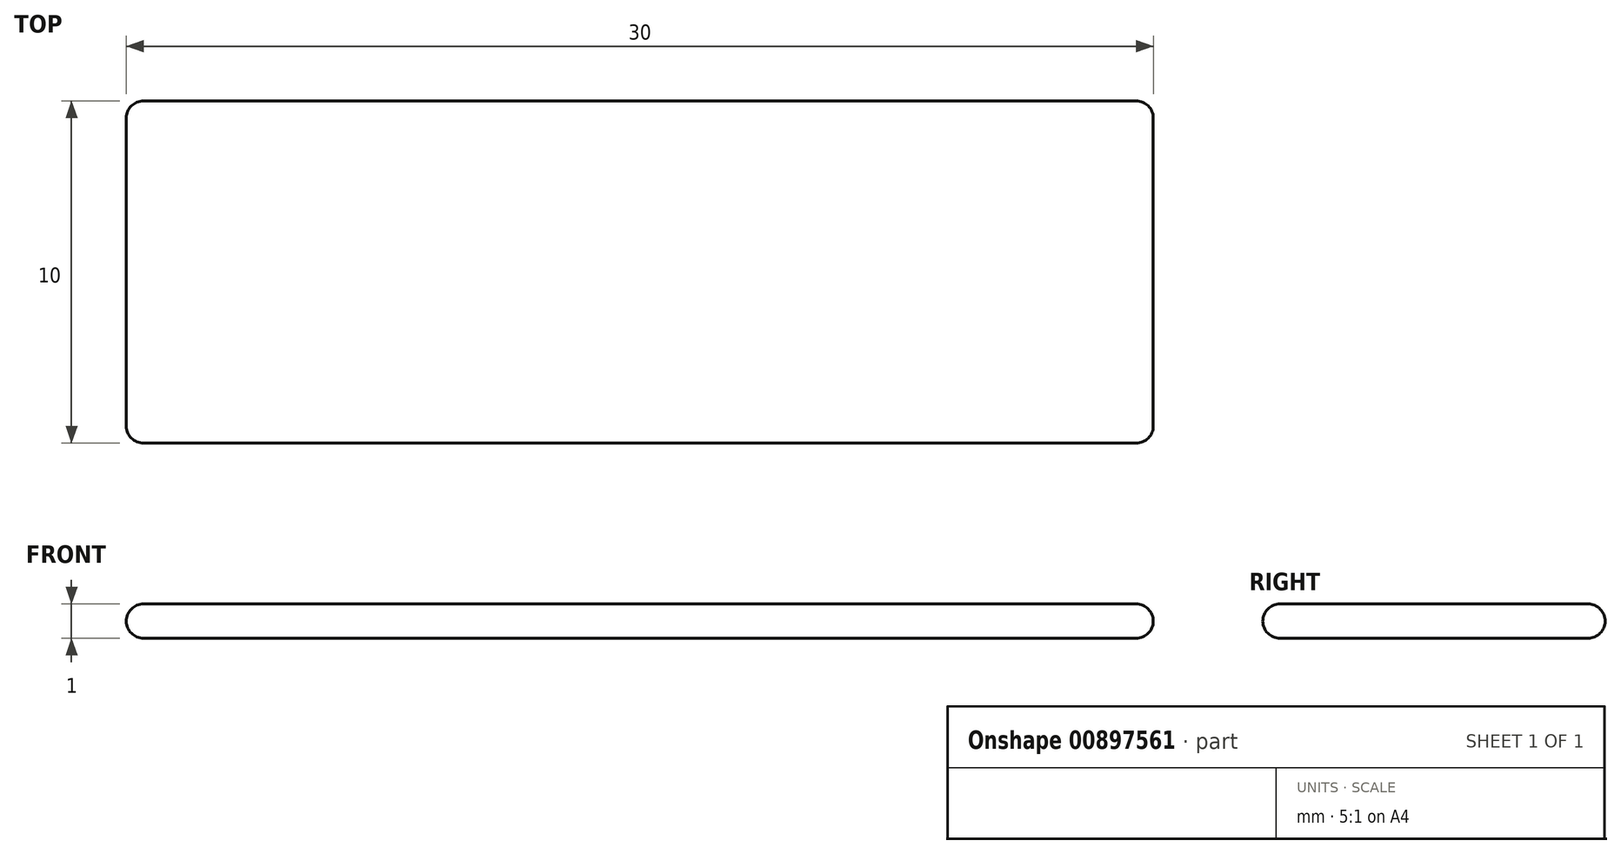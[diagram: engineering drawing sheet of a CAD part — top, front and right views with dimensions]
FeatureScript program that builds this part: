
annotation { "Feature Type Name" : "Feature", "Feature Type Description" : "" }
export const myFeature = defineFeature(function(context is Context, id is Id, definition is map)
    precondition{}
    {
        {
            var Q0;
            Q0=qCreatedBy(makeId("Top.planeOp"),FACE);
            var sketch = newSketch(context, id + "F0", { "sketchPlane" : qUnion([Q0])});
            skLineSegment(sketch, "E0.bottom", {"start": v(-49.18, 35.23) * mm, "end": v(-19.18, 35.23) * mm});
            skLineSegment(sketch, "E0.top", {"start": v(-49.18, 25.23) * mm, "end": v(-19.18, 25.23) * mm});
            skLineSegment(sketch, "E0.left", {"start": v(-49.18, 35.23) * mm, "end": v(-49.18, 25.23) * mm});
            skLineSegment(sketch, "E0.right", {"start": v(-19.18, 35.23) * mm, "end": v(-19.18, 25.23) * mm});
            skSolve(sketch);
        }
        {
            var Q0;
            Q0 = qSketchRegion(id + "F0", true);
            extrude(context, id + "F1", {"entities" : qUnion([Q0]), "depth" : 1 * mm, "offsetDistance" : 25 * mm});
        }
        {
            var Q0;
            Q0=makeQuery(id+"F1.opExtrude","CAP_EDGE",EDGE,{"disambiguationData":[OSD([sQuery(id+"F0.wireOp",EDGE,"E0.bottom")])],"isStart":false});
            var Q1;
            Q1=makeQuery(id+"F1.opExtrude","CAP_EDGE",EDGE,{"disambiguationData":[OSD([sQuery(id+"F0.wireOp",EDGE,"E0.left")])],"isStart":false});
            var Q2;
            Q2=makeQuery(id+"F1.opExtrude","CAP_EDGE",EDGE,{"disambiguationData":[OSD([sQuery(id+"F0.wireOp",EDGE,"E0.top")])],"isStart":false});
            var Q3;
            Q3=makeQuery(id+"F1.opExtrude","CAP_EDGE",EDGE,{"disambiguationData":[OSD([sQuery(id+"F0.wireOp",EDGE,"E0.right")])],"isStart":false});
            var Q4;
            Q4=makeQuery(id+"F1.opExtrude","SWEPT_EDGE",EDGE,{"disambiguationData":[OSD([sQuery(id+"F0.wireOp",EDGE,"E0.bottom"),sQuery(id+"F0.wireOp",EDGE,"E0.right")])]});
            var Q5;
            Q5=makeQuery(id+"F1.opExtrude","CAP_EDGE",EDGE,{"disambiguationData":[OSD([sQuery(id+"F0.wireOp",EDGE,"E0.bottom")])],"isStart":true});
            var Q6;
            Q6=makeQuery(id+"F1.opExtrude","SWEPT_EDGE",EDGE,{"disambiguationData":[OSD([sQuery(id+"F0.wireOp",EDGE,"E0.bottom"),sQuery(id+"F0.wireOp",EDGE,"E0.left")])]});
            var Q7;
            Q7=makeQuery(id+"F1.opExtrude","CAP_EDGE",EDGE,{"disambiguationData":[OSD([sQuery(id+"F0.wireOp",EDGE,"E0.left")])],"isStart":true});
            var Q8;
            Q8=makeQuery(id+"F1.opExtrude","SWEPT_EDGE",EDGE,{"disambiguationData":[OSD([sQuery(id+"F0.wireOp",EDGE,"E0.top"),sQuery(id+"F0.wireOp",EDGE,"E0.left")])]});
            var Q9;
            Q9=makeQuery(id+"F1.opExtrude","CAP_EDGE",EDGE,{"disambiguationData":[OSD([sQuery(id+"F0.wireOp",EDGE,"E0.top")])],"isStart":true});
            var Q10;
            Q10=makeQuery(id+"F1.opExtrude","SWEPT_EDGE",EDGE,{"disambiguationData":[OSD([sQuery(id+"F0.wireOp",EDGE,"E0.top"),sQuery(id+"F0.wireOp",EDGE,"E0.right")])]});
            var Q11;
            Q11=makeQuery(id+"F1.opExtrude","CAP_EDGE",EDGE,{"disambiguationData":[OSD([sQuery(id+"F0.wireOp",EDGE,"E0.right")])],"isStart":true});
            fillet(context, id + "F2", {"entities" : qUnion([Q0, Q1, Q2, Q3, Q4, Q5, Q6, Q7, Q8, Q9, Q10, Q11]), "radius" : 0.5 * mm, "tangentPropagation" : true, "allowEdgeOverflow" : false});
        }
    });
